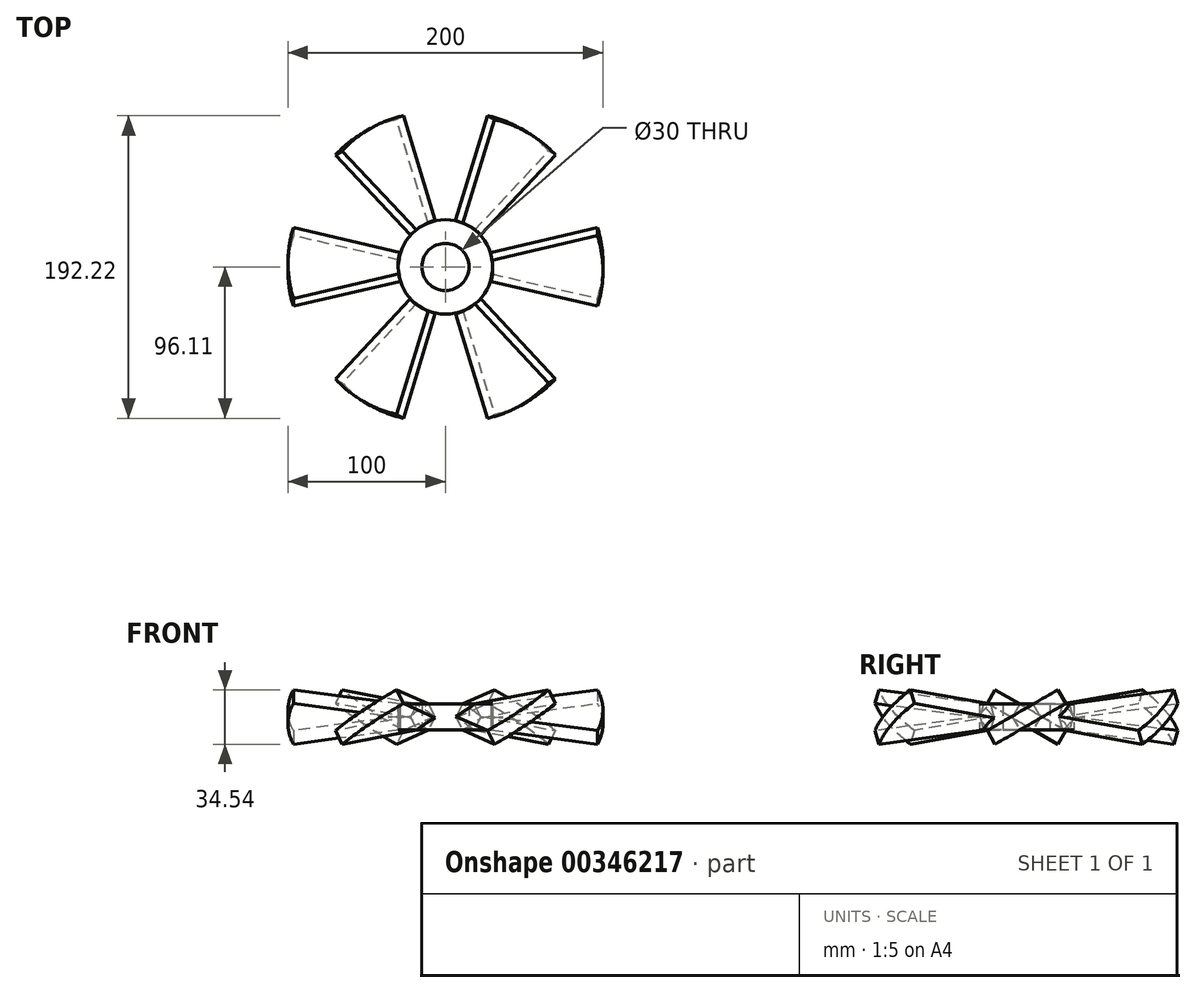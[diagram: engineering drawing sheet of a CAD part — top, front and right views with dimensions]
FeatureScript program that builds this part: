
annotation { "Feature Type Name" : "Feature", "Feature Type Description" : "" }
export const myFeature = defineFeature(function(context is Context, id is Id, definition is map)
    precondition{}
    {
        {
            var Q0;
            Q0=qCreatedBy(makeId("Top.planeOp"),FACE);
            var sketch = newSketch(context, id + "F0", { "sketchPlane" : qUnion([Q0])});
            skCircle(sketch, "E0", {"center": v(0, 0) * mm, "radius": 100 * mm});
            skCircle(sketch, "E1", {"center": v(0, 0) * mm, "radius": 30 * mm});
            skCircle(sketch, "E2", {"center": v(0, 0) * mm, "radius": 15 * mm});
            skLineSegment(sketch, "E3", {"start": v(0, 0) * mm, "end": v(100, 0) * mm});
            skLineSegment(sketch, "E4", {"start": v(0, 0) * mm, "end": v(96.6, 25.88) * mm});
            skLineSegment(sketch, "E5.MirrorCS", {"start": v(0, 0) * mm, "end": v(96.6, -25.88) * mm});
            skSolve(sketch);
        }
        {
            var Q0;
            {var subQ0=sQuery(id+"F0.wireOp",EDGE,"E3");var subQ1=sQuery(id+"F0.wireOp",EDGE,"E0");var subQ2=makeQuery(id+"F0.imprint","INTERSECT",VERTEX,{"derivedFrom":[subQ1,subQ0]});Q0=makeQuery(id+"F0.imprint","IMPRINT",FACE,{"disambiguationData":[TD([[makeQuery(id+"F0.imprint","IMPRINT",EDGE,{"disambiguationData":[TD([[subQ2,-1.0]])],"derivedFrom":subQ1}),1.0]])]});}
            var Q1;
            {var subQ0=sQuery(id+"F0.wireOp",EDGE,"E3");var subQ1=sQuery(id+"F0.wireOp",EDGE,"E0");var subQ2=makeQuery(id+"F0.imprint","INTERSECT",VERTEX,{"derivedFrom":[subQ1,subQ0]});Q1=makeQuery(id+"F0.imprint","IMPRINT",FACE,{"disambiguationData":[TD([[makeQuery(id+"F0.imprint","IMPRINT",EDGE,{"disambiguationData":[TD([[subQ2,1.0]])],"derivedFrom":subQ1}),1.0]])]});}
            extrude(context, id + "F1", {"entities" : qUnion([Q0, Q1]), "depth" : 5 * mm, "hasSecondDirection" : true, "secondDirectionOppositeDirection" : true, "secondDirectionDepth" : 5 * mm});
        }
        {
            var Q0;
            Q0=makeQuery(id+"F1.opExtrude","SWEPT_BODY",BODY,{"disambiguationData":[OSD([sQuery(id+"F0.wireOp",EDGE,"E0"),sQuery(id+"F0.wireOp",EDGE,"E1"),sQuery(id+"F0.wireOp",EDGE,"E4"),sQuery(id+"F0.wireOp",EDGE,"E5.MirrorCS")])]});
            var Q1;
            Q1=sQuery(id+"F0.wireOp",EDGE,"E3");
            var Q2;
            Q2=sQuery(id+"F0.wireOp",EDGE,"E3");
            transform(context, id + "F2", {"entities" : qUnion([Q0]), "transformType" : TransformType.ROTATION, "transformAxis" : qUnion([Q2]), "angle" : 30 * degree, "makeCopy" : false});
        }
        {
            var Q0;
            Q0=qCreatedBy(makeId("Front.planeOp"),FACE);
            var sketch = newSketch(context, id + "F3", { "sketchPlane" : qUnion([Q0])});
            skLineSegment(sketch, "E6", {"start": v(0, 0) * mm, "end": v(0, 67.77) * mm});
            skSolve(sketch);
        }
        {
            var Q0;
            Q0=makeQuery(id+"F1.opExtrude","SWEPT_BODY",BODY,{"disambiguationData":[OSD([sQuery(id+"F0.wireOp",EDGE,"E0"),sQuery(id+"F0.wireOp",EDGE,"E1"),sQuery(id+"F0.wireOp",EDGE,"E4"),sQuery(id+"F0.wireOp",EDGE,"E5.MirrorCS")])]});
            var Q1;
            Q1=sQuery(id+"F3.wireOp",EDGE,"E6");
            circularPattern(context, id + "F4", {"entities" : qUnion([Q0]), "axis" : qUnion([Q1]), "angle" : 360 * degree, "instanceCount" : 6, "equalSpace" : true});
        }
        {
            var Q0;
            {var subQ0=sQuery(id+"F0.wireOp",EDGE,"E4");var subQ1=sQuery(id+"F0.wireOp",EDGE,"E1");var subQ2=makeQuery(id+"F0.imprint","INTERSECT",VERTEX,{"derivedFrom":[subQ1,subQ0]});Q0=makeQuery(id+"F0.imprint","IMPRINT",FACE,{"disambiguationData":[TD([[makeQuery(id+"F0.imprint","IMPRINT",EDGE,{"disambiguationData":[TD([[subQ2,-1.0]])],"derivedFrom":subQ1}),1.0]])]});}
            var Q1;
            {var subQ0=sQuery(id+"F0.wireOp",EDGE,"E4");var subQ1=sQuery(id+"F0.wireOp",EDGE,"E1");var subQ2=makeQuery(id+"F0.imprint","INTERSECT",VERTEX,{"derivedFrom":[subQ1,subQ0]});Q1=makeQuery(id+"F0.imprint","IMPRINT",FACE,{"disambiguationData":[TD([[makeQuery(id+"F0.imprint","IMPRINT",EDGE,{"disambiguationData":[TD([[subQ2,1.0]])],"derivedFrom":subQ1}),1.0]])]});}
            var Q2;
            {var subQ0=sQuery(id+"F0.wireOp",EDGE,"E3");var subQ1=sQuery(id+"F0.wireOp",EDGE,"E1");var subQ2=makeQuery(id+"F0.imprint","INTERSECT",VERTEX,{"derivedFrom":[subQ1,subQ0]});Q2=makeQuery(id+"F0.imprint","IMPRINT",FACE,{"disambiguationData":[TD([[makeQuery(id+"F0.imprint","IMPRINT",EDGE,{"disambiguationData":[TD([[subQ2,1.0]])],"derivedFrom":subQ1}),1.0]])]});}
            var Q3;
            Q3=makeQuery(id+"F4.opPattern","COPY",VERTEX,{"derivedFrom":makeQuery(id+"F1.opExtrude","CAP_VERTEX",VERTEX,{"disambiguationData":[OSD([sQuery(id+"F0.wireOp",EDGE,"E1"),sQuery(id+"F0.wireOp",EDGE,"E4")])],"isStart":false}),"instanceName":"1"});
            var Q4;
            Q4=makeQuery(id+"F4.opPattern","COPY",VERTEX,{"derivedFrom":makeQuery(id+"F1.opExtrude","CAP_VERTEX",VERTEX,{"disambiguationData":[OSD([sQuery(id+"F0.wireOp",EDGE,"E1"),sQuery(id+"F0.wireOp",EDGE,"E5.MirrorCS")])],"isStart":true}),"instanceName":"5"});
            extrude(context, id + "F5", {"entities" : qUnion([Q0, Q1, Q2]), "endBound" : BoundingType.UP_TO_VERTEX, "endBoundEntityVertex" : qUnion([Q3]), "depth" : 25 * mm, "hasSecondDirection" : true, "secondDirectionBound" : SecondDirectionBoundingType.UP_TO_VERTEX, "secondDirectionOppositeDirection" : true, "secondDirectionBoundEntityVertex" : qUnion([Q4]), "secondDirectionDepth" : 25 * mm});
        }
    });
